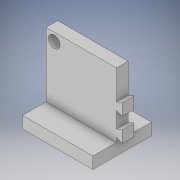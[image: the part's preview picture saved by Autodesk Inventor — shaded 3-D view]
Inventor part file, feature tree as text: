
AUTODESK INVENTOR PART (.ipt)
format: ipt  version: 2019 (Build 230136000, 136)  size: 144,384 bytes
history: native  units: in
note: dims shown in document units (in); Inventor stores cm internally (conversion verified against a paired STEP export)
features: sketch x4, extrude x3, fillet x1
ambient origin geometry x8: Origin, YZ Plane, XZ Plane, XY Plane, X Axis, Y Axis, Z Axis, Center Point
bodies: Solid1 (feature_tree)
feature tree (8):
  extrude  "Extrusion1"  Depth=2.3622in
  sketch  "Sketch2"  dims[d2=0.3937in d3=0.481in d4=0.481in d5=0.1969in d6=0.2504in]
  sketch  "Sketch3"  dims[d7=0.1969in d8=0.7874in]
  extrude  "Extrusion2"  Depth=0.1969in
  fillet  "Fillet1"  Radius=0.2504in
  extrude  "Extrusion3"  Depth=0.7874in
  sketch  "Sketch1"  dims[d0=2.5591in d1=2.3622in]
  sketch  "Sketch4"  dims[d9=0.481in d10=0.481in d11=0.537in d12=0.3937in d13=0.481in d14=0.481in d15=0.481in d16=0.1969in d17=1.5748in d18=0.3937in d19=0.2756in d20=0.2756in d21=0.3937in d22=0.0in d23=0.3937in d24=0.7874in d25=0.0in d26=0.1181in d27=0.7874in d28=0.0in]
